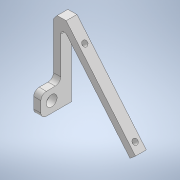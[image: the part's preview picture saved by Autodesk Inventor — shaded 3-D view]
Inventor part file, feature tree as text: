
AUTODESK INVENTOR PART (.ipt)
format: ipt  version: 2020 (Build 240168000, 168)  size: 167,936 bytes
history: native  units: mm
features: extrude x3, thicken_offset x3, sketch x3, fillet x2, projected_geometry x2, chamfer x1
ambient origin geometry x8: Origin, YZ Plane, XZ Plane, XY Plane, X Axis, Y Axis, Z Axis, Center Point
bodies: Solid1 (feature_tree)
feature tree (14):
  extrude  "Extrusion1"  Depth=40.0mm
  fillet  "Fillet1"  Radius=60.0mm
  extrude  "Extrusion2"  Depth=60.0mm
  extrude  "Extrusion3"  Depth=2.0mm
  fillet  "Fillet2"  Radius=6.0mm
  thicken_offset  "Thicken1"
  thicken_offset  "Thicken2"
  thicken_offset  "Thicken3"
  chamfer  "Chamfer1"  Distance=2.0mm
  sketch  "Sketch1"  dims[d0=4.0mm d1=40.0mm d2=60.0mm]
  sketch  "Sketch2"  dims[d3=4.0mm d4=60.0mm]
  projected_geometry  "Projected Loop1"
  sketch  "Sketch3"  dims[d5=4.0mm d6=6.981317mm d7=6.0mm d8=0.0mm d9=2.0mm d10=5.0mm d11=43.5mm d12=3.0mm d13=3.0mm d14=6.0mm d15=0.0mm d16=16.0mm d17=10.0mm d18=5.0mm d19=6.0mm d20=6.0mm d21=0.0mm d22=3.0mm d23=1.0mm d24=1.0mm d25=1.0mm d26=1.0mm d27=1.0mm d28=1.0mm d29=4.0mm d30=2.0mm d31=45.0deg]
  projected_geometry  "Projected Loop2"
